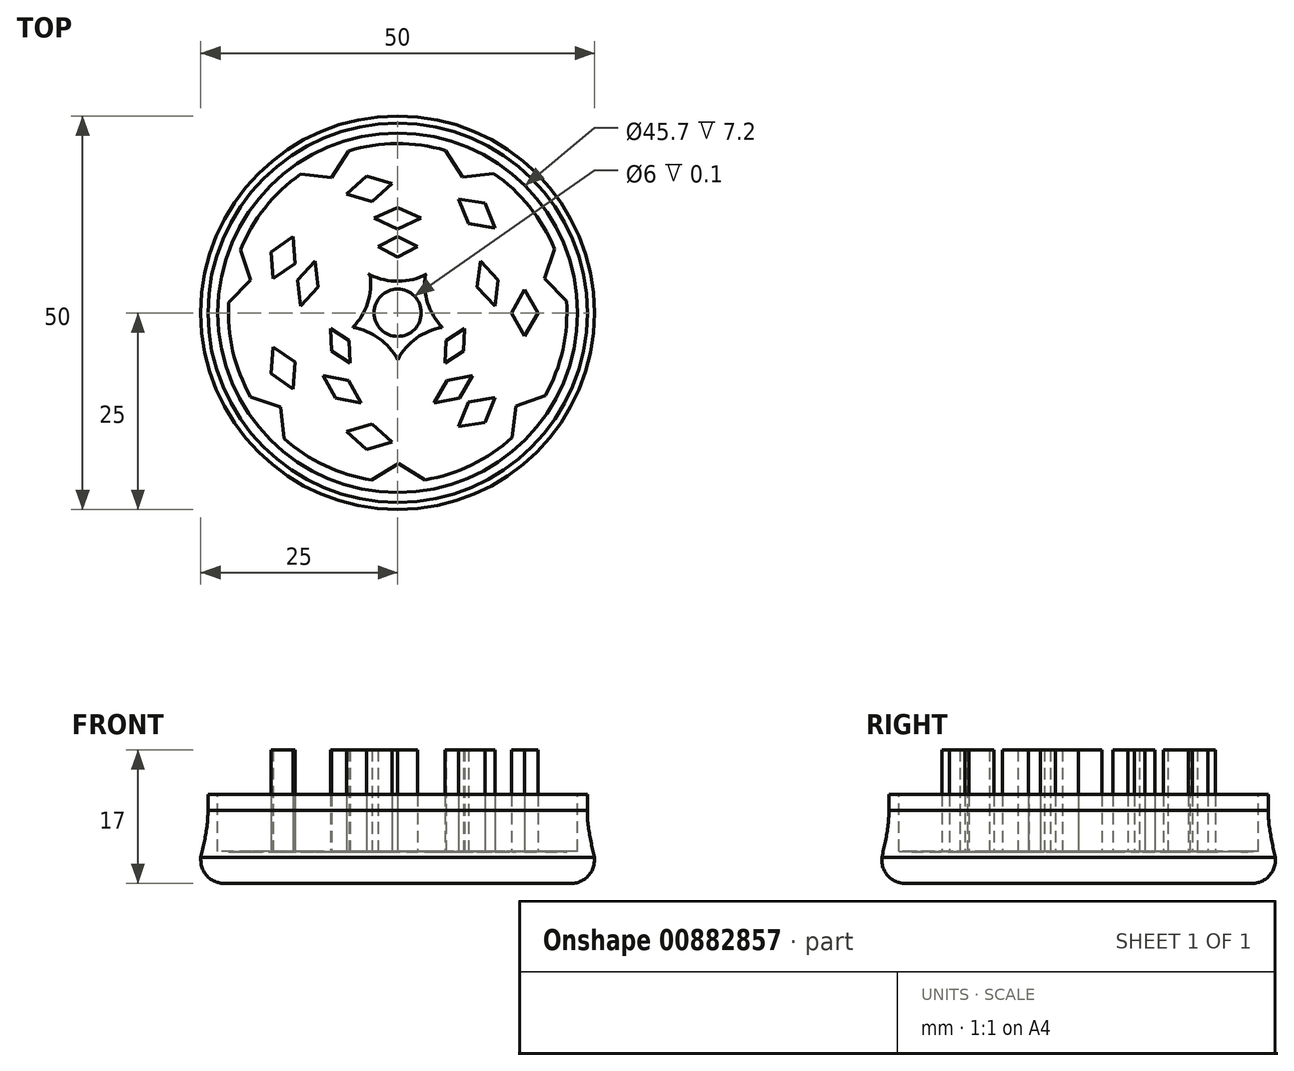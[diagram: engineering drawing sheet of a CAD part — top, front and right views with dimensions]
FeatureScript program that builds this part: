
annotation { "Feature Type Name" : "Feature", "Feature Type Description" : "" }
export const myFeature = defineFeature(function(context is Context, id is Id, definition is map)
    precondition{}
    {
        {
            var Q0;
            Q0=qCreatedBy(makeId("Top.planeOp"),FACE);
            var sketch = newSketch(context, id + "F0", { "sketchPlane" : qUnion([Q0])});
            skCircle(sketch, "E0", {"center": v(0, 0) * mm, "radius": 25 * mm});
            skSolve(sketch);
        }
        {
            var Q0;
            Q0 = qSketchRegion(id + "F0", true);
            extrude(context, id + "F1", {"entities" : qUnion([Q0]), "depth" : 15 * mm, "offsetDistance" : 25 * mm});
        }
        {
            var Q0;
            Q0=makeQuery(id+"F1.opExtrude","CAP_EDGE",EDGE,{"disambiguationData":[OSD([sQuery(id+"F0.wireOp",EDGE,"E0")])],"isStart":true});
            fillet(context, id + "F2", {"entities" : qUnion([Q0]), "radius" : 3 * mm, "tangentPropagation" : true, "allowEdgeOverflow" : false});
        }
        {
            var Q0;
            Q0=qCreatedBy(makeId("Front.planeOp"),FACE);
            var sketch = newSketch(context, id + "F3", { "sketchPlane" : qUnion([Q0])});
            skLineSegment(sketch, "E1", {"start": v(0, 23.25) * mm, "end": v(0, 17.15) * mm});
            skLineSegment(sketch, "E2", {"start": v(0, 17.15) * mm, "end": v(0, 14.94) * mm});
            skLineSegment(sketch, "E3", {"start": v(0, 14.94) * mm, "end": v(25, 14.94) * mm});
            skFitSpline(sketch, "E4", {"points": [v(25, 14.94) * mm, v(24.1, 9.2) * mm, v(25, 3.32) * mm], "startDerivative": vector(-2.73, -11.51) * mm, "endDerivative": vector(2.72, -11.72) * mm});
            skLineSegment(sketch, "E5", {"start": v(25, 3.32) * mm, "end": v(27.42, 5.28) * mm});
            skLineSegment(sketch, "E6", {"start": v(27.42, 5.28) * mm, "end": v(25, 14.94) * mm});
            skSolve(sketch);
        }
        {
            var Q0;
            Q0=makeQuery(id+"F3.imprint","IMPRINT",FACE,{"disambiguationData":[TD([[makeQuery(id+"F3.imprint","IMPRINT",EDGE,{"derivedFrom":sQuery(id+"F3.wireOp",EDGE,"E4")}),1.0]])]});
            var Q1;
            Q1=sQuery(id+"F3.wireOp",EDGE,"E1");
            revolve(context, id + "F4", {"operationType" : NewBodyOperationType.REMOVE, "surfaceOperationType" : NewSurfaceOperationType.NEW, "entities" : qUnion([Q0]), "axis" : qUnion([Q1]), "revolveType" : RevolveType.FULL, "oppositeDirection" : true});
        }
        {
            var Q0;
            Q0=makeQuery(id+"F1.opExtrude","CAP_FACE",FACE,{"disambiguationData":[OSD([sQuery(id+"F0.wireOp",EDGE,"E0")])],"isStart":false});
            var sketch = newSketch(context, id + "F5", { "sketchPlane" : qUnion([Q0])});
            skCircle(sketch, "E7", {"center": v(0, 0) * mm, "radius": 21.5 * mm});
            skSolve(sketch);
        }
        {
            var Q0;
            Q0 = qSketchRegion(id + "F5", true);
            extrude(context, id + "F6", {"entities" : qUnion([Q0]), "operationType" : NewBodyOperationType.REMOVE, "oppositeDirection" : true, "depth" : 11 * mm, "offsetDistance" : 25 * mm});
        }
        {
            var Q0;
            Q0=makeQuery(id+"F6.boolean.opBoolean","COPY",FACE,{"derivedFrom":makeQuery(id+"F6.opExtrude","CAP_FACE",FACE,{"disambiguationData":[OSD([sQuery(id+"F5.wireOp",EDGE,"E7")])],"isStart":false})});
            var sketch = newSketch(context, id + "F7", { "sketchPlane" : qUnion([Q0])});
            skCircle(sketch, "E8.cCircle", {"center": v(0, 0) * mm, "radius": 4.82 * mm, "construction": true});
            skLineSegment(sketch, "E8.0", {"start": v(-3.5, 4.82) * mm, "end": v(-3.5, 4.82) * mm});
            skLineSegment(sketch, "E8.1", {"start": v(3.5, 4.82) * mm, "end": v(3.5, 4.81) * mm});
            skLineSegment(sketch, "E8.2", {"start": v(5.66, -1.84) * mm, "end": v(5.66, -1.84) * mm});
            skLineSegment(sketch, "E8.3", {"start": v(0, -5.95) * mm, "end": v(-2.83, -3.9) * mm});
            skLineSegment(sketch, "E8.4", {"start": v(-5.66, -1.84) * mm, "end": v(-5.66, -1.83) * mm});
            skPoint(sketch, "E8.0.midPoint", {"position": v(0, 4.82) * mm});
            skCircle(sketch, "E9", {"center": v(0, 0) * mm, "radius": 3 * mm});
            skLineSegment(sketch, "E10", {"start": v(-3.69, 4.91) * mm, "end": v(-3.5, 4.82) * mm});
            skLineSegment(sketch, "E11", {"start": v(3.5, 4.82) * mm, "end": v(3.69, 4.91) * mm});
            skPoint(sketch, "E12.visualSharp", {"position": v(0, 3) * mm});
            skArc(sketch, "E12.filletArc", {"start": v(-3.69, 4.91) * mm, "mid": v(0, 4.01) * mm, "end": v(3.69, 4.91) * mm});
            skArc(sketch, "E13.1.0", {"start": v(-5.81, -1.99) * mm, "mid": v(-3.82, 1.24) * mm, "end": v(-3.53, 5.02) * mm});
            skArc(sketch, "E13.2.0", {"start": v(0.1, -6.14) * mm, "mid": v(-2.36, -3.25) * mm, "end": v(-5.87, -1.8) * mm});
            skArc(sketch, "E13.3.0", {"start": v(5.87, -1.8) * mm, "mid": v(2.36, -3.25) * mm, "end": v(-0.1, -6.14) * mm});
            skArc(sketch, "E13.4.0", {"start": v(3.53, 5.02) * mm, "mid": v(3.82, 1.24) * mm, "end": v(5.81, -1.99) * mm});
            skLineSegment(sketch, "E14.trimOffspring", {"start": v(4.58, 1.49) * mm, "end": v(5.66, -1.84) * mm});
            skLineSegment(sketch, "E15.trimOffspring", {"start": v(2.83, -3.9) * mm, "end": v(0, -5.95) * mm});
            skLineSegment(sketch, "E16.trimOffspring", {"start": v(-5.66, -1.84) * mm, "end": v(-5.66, -1.84) * mm});
            skLineSegment(sketch, "E17.trimOffspring", {"start": v(-4.58, 1.49) * mm, "end": v(-3.5, 4.82) * mm});
            skLineSegment(sketch, "E18", {"start": v(0, 0) * mm, "end": v(0, 12.01) * mm});
            skLineSegment(sketch, "E19", {"start": v(0, 12.01) * mm, "end": v(3, 12.01) * mm});
            skLineSegment(sketch, "E20", {"start": v(3, 12.01) * mm, "end": v(0, 10.64) * mm});
            skLineSegment(sketch, "E21.MirrorCS", {"start": v(3, 12.01) * mm, "end": v(0, 13.4) * mm});
            skLineSegment(sketch, "E22.MirrorCS", {"start": v(-3, 12.01) * mm, "end": v(0, 10.64) * mm});
            skLineSegment(sketch, "E23.MirrorCS", {"start": v(-3, 12.01) * mm, "end": v(0, 13.4) * mm});
            skLineSegment(sketch, "E24.1.0", {"start": v(-12.35, 0.86) * mm, "end": v(-10.12, 3.29) * mm});
            skLineSegment(sketch, "E24.1.1", {"start": v(-10.5, 6.57) * mm, "end": v(-10.12, 3.29) * mm});
            skLineSegment(sketch, "E24.1.2", {"start": v(-10.5, 6.57) * mm, "end": v(-12.74, 4.14) * mm});
            skLineSegment(sketch, "E24.1.3", {"start": v(-12.35, 0.86) * mm, "end": v(-12.74, 4.14) * mm});
            skLineSegment(sketch, "E24.2.0", {"start": v(-4.63, -11.48) * mm, "end": v(-6.25, -8.6) * mm});
            skLineSegment(sketch, "E24.2.1", {"start": v(-9.49, -7.96) * mm, "end": v(-6.25, -8.6) * mm});
            skLineSegment(sketch, "E24.2.2", {"start": v(-9.49, -7.96) * mm, "end": v(-7.87, -10.83) * mm});
            skLineSegment(sketch, "E24.2.3", {"start": v(-4.63, -11.48) * mm, "end": v(-7.87, -10.83) * mm});
            skLineSegment(sketch, "E24.3.0", {"start": v(9.49, -7.96) * mm, "end": v(6.25, -8.6) * mm});
            skLineSegment(sketch, "E24.3.1", {"start": v(4.63, -11.48) * mm, "end": v(6.25, -8.6) * mm});
            skLineSegment(sketch, "E24.3.2", {"start": v(4.63, -11.48) * mm, "end": v(7.87, -10.83) * mm});
            skLineSegment(sketch, "E24.3.3", {"start": v(9.49, -7.96) * mm, "end": v(7.87, -10.83) * mm});
            skLineSegment(sketch, "E24.4.0", {"start": v(10.5, 6.57) * mm, "end": v(10.12, 3.29) * mm});
            skLineSegment(sketch, "E24.4.1", {"start": v(12.35, 0.86) * mm, "end": v(10.12, 3.29) * mm});
            skLineSegment(sketch, "E24.4.2", {"start": v(12.35, 0.86) * mm, "end": v(12.74, 4.14) * mm});
            skLineSegment(sketch, "E24.4.3", {"start": v(10.5, 6.57) * mm, "end": v(12.74, 4.14) * mm});
            skLineSegment(sketch, "E25", {"start": v(0, 0) * mm, "end": v(0.1, -21.5) * mm});
            skLineSegment(sketch, "E26", {"start": v(0.1, -21.5) * mm, "end": v(3.92, -21.48) * mm});
            skLineSegment(sketch, "E27", {"start": v(3.92, -21.48) * mm, "end": v(0.08, -19.13) * mm});
            skLineSegment(sketch, "E28.MirrorCS", {"start": v(-3.73, -21.52) * mm, "end": v(0.08, -19.13) * mm});
            skLineSegment(sketch, "E29.MirrorCS", {"start": v(0.1, -21.5) * mm, "end": v(-3.73, -21.52) * mm});
            skLineSegment(sketch, "E30.1.0", {"start": v(19.24, -10.33) * mm, "end": v(15, -11.86) * mm});
            skLineSegment(sketch, "E30.1.1", {"start": v(14.5, -16.33) * mm, "end": v(15, -11.86) * mm});
            skLineSegment(sketch, "E30.1.2", {"start": v(16.87, -13.33) * mm, "end": v(19.24, -10.33) * mm});
            skLineSegment(sketch, "E30.1.3", {"start": v(16.87, -13.33) * mm, "end": v(14.5, -16.33) * mm});
            skLineSegment(sketch, "E30.2.0", {"start": v(20.07, 8.6) * mm, "end": v(18.63, 4.34) * mm});
            skLineSegment(sketch, "E30.2.1", {"start": v(21.8, 1.15) * mm, "end": v(18.63, 4.34) * mm});
            skLineSegment(sketch, "E30.2.2", {"start": v(20.94, 4.88) * mm, "end": v(20.07, 8.6) * mm});
            skLineSegment(sketch, "E30.2.3", {"start": v(20.94, 4.88) * mm, "end": v(21.8, 1.15) * mm});
            skLineSegment(sketch, "E30.3.0", {"start": v(5.8, 21.06) * mm, "end": v(8.22, 17.27) * mm});
            skLineSegment(sketch, "E30.3.1", {"start": v(12.7, 17.77) * mm, "end": v(8.22, 17.27) * mm});
            skLineSegment(sketch, "E30.3.2", {"start": v(9.24, 19.41) * mm, "end": v(5.8, 21.06) * mm});
            skLineSegment(sketch, "E30.3.3", {"start": v(9.24, 19.41) * mm, "end": v(12.7, 17.77) * mm});
            skLineSegment(sketch, "E30.4.0", {"start": v(-12.85, 17.66) * mm, "end": v(-8.37, 17.2) * mm});
            skLineSegment(sketch, "E30.4.1", {"start": v(-5.98, 21) * mm, "end": v(-8.37, 17.2) * mm});
            skLineSegment(sketch, "E30.4.2", {"start": v(-9.41, 19.33) * mm, "end": v(-12.85, 17.66) * mm});
            skLineSegment(sketch, "E30.4.3", {"start": v(-9.41, 19.33) * mm, "end": v(-5.98, 21) * mm});
            skLineSegment(sketch, "E30.5.0", {"start": v(-21.82, 0.96) * mm, "end": v(-18.67, 4.17) * mm});
            skLineSegment(sketch, "E30.5.1", {"start": v(-20.15, 8.42) * mm, "end": v(-18.67, 4.17) * mm});
            skLineSegment(sketch, "E30.5.2", {"start": v(-20.98, 4.7) * mm, "end": v(-21.82, 0.96) * mm});
            skLineSegment(sketch, "E30.5.3", {"start": v(-20.98, 4.7) * mm, "end": v(-20.15, 8.42) * mm});
            skLineSegment(sketch, "E30.6.0", {"start": v(-14.35, -16.46) * mm, "end": v(-14.9, -12) * mm});
            skLineSegment(sketch, "E30.6.1", {"start": v(-19.15, -10.5) * mm, "end": v(-14.9, -12) * mm});
            skLineSegment(sketch, "E30.6.2", {"start": v(-16.75, -13.48) * mm, "end": v(-14.35, -16.46) * mm});
            skLineSegment(sketch, "E30.6.3", {"start": v(-16.75, -13.48) * mm, "end": v(-19.15, -10.5) * mm});
            skSolve(sketch);
        }
        {
            var Q0;
            Q0 = qSketchRegion(id + "F7", true);
            extrude(context, id + "F8", {"entities" : qUnion([Q0]), "operationType" : NewBodyOperationType.ADD, "depth" : 10.8 * mm, "offsetDistance" : 25 * mm});
        }
        {
            var Q0;
            Q0=makeQuery(id+"F1.opExtrude","CAP_FACE",FACE,{"disambiguationData":[OSD([sQuery(id+"F0.wireOp",EDGE,"E0")])],"isStart":false});
            var sketch = newSketch(context, id + "F9", { "sketchPlane" : qUnion([Q0])});
            skCircle(sketch, "E31", {"center": v(0, 0) * mm, "radius": 26.73 * mm});
            skSolve(sketch);
        }
        {
            var Q0;
            Q0 = qSketchRegion(id + "F9", true);
            extrude(context, id + "F10", {"entities" : qUnion([Q0]), "operationType" : NewBodyOperationType.REMOVE, "oppositeDirection" : true, "depth" : 5.7 * mm, "offsetDistance" : 25 * mm});
        }
        {
            var Q0;
            Q0=makeQuery(id+"F10.boolean.opBoolean","COPY",FACE,{"disambiguationData":[TD([makeQuery(id+"F8.opExtrude","SWEPT_FACE",FACE,{"disambiguationData":[OSD([sQuery(id+"F7.wireOp",EDGE,"E9")])]})])],"derivedFrom":makeQuery(id+"F10.opExtrude","CAP_FACE",FACE,{"disambiguationData":[OSD([sQuery(id+"F9.wireOp",EDGE,"E31")])],"isStart":false})});
            var sketch = newSketch(context, id + "F11", { "sketchPlane" : qUnion([Q0])});
            skCircle(sketch, "E32", {"center": v(0, 0) * mm, "radius": 22.85 * mm});
            skSolve(sketch);
        }
        {
            var Q0;
            Q0=makeQuery(id+"F11.imprint","IMPRINT",FACE,{"disambiguationData":[TD([[makeQuery(id+"F11.imprint","IMPRINT",EDGE,{"derivedFrom":sQuery(id+"F11.wireOp",EDGE,"E32")}),1.0]])]});
            var Q1;
            {var subQ0=makeQuery(id+"F10.opExtrude","CAP_FACE",FACE,{"disambiguationData":[OSD([sQuery(id+"F9.wireOp",EDGE,"E31")])],"isStart":false});Q1=makeQuery(id+"F11.imprint","IMPRINT",FACE,{"disambiguationData":[TD([[makeQuery(id+"F11.imprint","IMPRINT",EDGE,{"derivedFrom":makeQuery(id+"F10.boolean.opBoolean","INTERSECT",EDGE,{"derivedFrom":[makeQuery(id+"F8.opExtrude","SWEPT_FACE",FACE,{"disambiguationData":[OSD([sQuery(id+"F7.wireOp",EDGE,"E9")])]}),subQ0]})}),-1.0]])]});}
            extrude(context, id + "F12", {"entities" : qUnion([Q0, Q1]), "operationType" : NewBodyOperationType.REMOVE, "oppositeDirection" : true, "depth" : 5.2 * mm, "offsetDistance" : 25 * mm});
        }
        {
            var Q0;
            {var subQ0=sQuery(id+"F5.wireOp",EDGE,"E7");Q0=makeQuery(id+"F8.boolean.opBoolean","SPLIT",FACE,{"disambiguationData":[TD([makeQuery(id+"F6.boolean.opBoolean","COPY",FACE,{"derivedFrom":makeQuery(id+"F6.opExtrude","SWEPT_FACE",FACE,{"disambiguationData":[OSD([subQ0])]})})])],"derivedFrom":makeQuery(id+"F6.boolean.opBoolean","COPY",FACE,{"derivedFrom":makeQuery(id+"F6.opExtrude","CAP_FACE",FACE,{"disambiguationData":[OSD([subQ0])],"isStart":false})})});}
            var sketch = newSketch(context, id + "F13", { "sketchPlane" : qUnion([Q0])});
            skCircle(sketch, "E33", {"center": v(0, 0) * mm, "radius": 6.14 * mm});
            skCircle(sketch, "E34", {"center": v(0, 0) * mm, "radius": 10.64 * mm});
            skCircle(sketch, "E35", {"center": v(0, 0) * mm, "radius": 13.4 * mm});
            skCircle(sketch, "E36", {"center": v(0, 0) * mm, "radius": 19.13 * mm});
            skLineSegment(sketch, "E37", {"start": v(0, 0) * mm, "end": v(0, 6.14) * mm});
            skLineSegment(sketch, "E38", {"start": v(0, 6.14) * mm, "end": v(0, 10.64) * mm});
            skLineSegment(sketch, "E39", {"start": v(0, 8.39) * mm, "end": v(2.5, 8.39) * mm});
            skLineSegment(sketch, "E40", {"start": v(2.5, 8.39) * mm, "end": v(0, 7.1) * mm});
            skLineSegment(sketch, "E41.MirrorCS", {"start": v(2.5, 8.39) * mm, "end": v(0, 9.67) * mm});
            skLineSegment(sketch, "E42.MirrorCS", {"start": v(-2.5, 8.39) * mm, "end": v(0, 9.67) * mm});
            skLineSegment(sketch, "E43.MirrorCS", {"start": v(-2.5, 8.39) * mm, "end": v(0, 7.1) * mm});
            skLineSegment(sketch, "E44.1.0", {"start": v(-6.02, -6.36) * mm, "end": v(-6.16, -3.55) * mm});
            skLineSegment(sketch, "E44.1.1", {"start": v(-8.52, -2.03) * mm, "end": v(-6.16, -3.55) * mm});
            skLineSegment(sketch, "E44.1.2", {"start": v(-6.02, -6.36) * mm, "end": v(-8.38, -4.84) * mm});
            skLineSegment(sketch, "E44.1.3", {"start": v(-8.52, -2.03) * mm, "end": v(-8.38, -4.84) * mm});
            skLineSegment(sketch, "E44.2.0", {"start": v(8.52, -2.03) * mm, "end": v(6.16, -3.55) * mm});
            skLineSegment(sketch, "E44.2.1", {"start": v(6.02, -6.36) * mm, "end": v(6.16, -3.55) * mm});
            skLineSegment(sketch, "E44.2.2", {"start": v(8.52, -2.03) * mm, "end": v(8.38, -4.84) * mm});
            skLineSegment(sketch, "E44.2.3", {"start": v(6.02, -6.36) * mm, "end": v(8.38, -4.84) * mm});
            skLineSegment(sketch, "E45", {"start": v(0, 0) * mm, "end": v(16.14, 0) * mm});
            skLineSegment(sketch, "E46", {"start": v(16.14, 0) * mm, "end": v(16.14, 2.95) * mm});
            skLineSegment(sketch, "E47", {"start": v(16.14, 2.95) * mm, "end": v(14.48, 0) * mm});
            skLineSegment(sketch, "E48.MirrorCS", {"start": v(16.14, 2.95) * mm, "end": v(17.81, 0) * mm});
            skLineSegment(sketch, "E49.MirrorCS", {"start": v(16.14, -2.95) * mm, "end": v(14.48, 0) * mm});
            skLineSegment(sketch, "E50.MirrorCS", {"start": v(16.14, -2.95) * mm, "end": v(17.81, 0) * mm});
            skLineSegment(sketch, "E51.1.0", {"start": v(7.76, 14.46) * mm, "end": v(9.03, 11.32) * mm});
            skLineSegment(sketch, "E51.1.1", {"start": v(12.37, 10.78) * mm, "end": v(9.03, 11.32) * mm});
            skLineSegment(sketch, "E51.1.2", {"start": v(12.37, 10.78) * mm, "end": v(11.1, 13.93) * mm});
            skLineSegment(sketch, "E51.1.3", {"start": v(7.76, 14.46) * mm, "end": v(11.1, 13.93) * mm});
            skLineSegment(sketch, "E51.2.0", {"start": v(-6.47, 15.08) * mm, "end": v(-3.22, 14.11) * mm});
            skLineSegment(sketch, "E51.2.1", {"start": v(-0.72, 16.4) * mm, "end": v(-3.22, 14.11) * mm});
            skLineSegment(sketch, "E51.2.2", {"start": v(-0.72, 16.4) * mm, "end": v(-3.96, 17.37) * mm});
            skLineSegment(sketch, "E51.2.3", {"start": v(-6.47, 15.08) * mm, "end": v(-3.96, 17.37) * mm});
            skLineSegment(sketch, "E51.3.0", {"start": v(-15.82, 4.35) * mm, "end": v(-13.04, 6.28) * mm});
            skLineSegment(sketch, "E51.3.1", {"start": v(-13.27, 9.66) * mm, "end": v(-13.04, 6.28) * mm});
            skLineSegment(sketch, "E51.3.2", {"start": v(-13.27, 9.66) * mm, "end": v(-16.05, 7.73) * mm});
            skLineSegment(sketch, "E51.3.3", {"start": v(-15.82, 4.35) * mm, "end": v(-16.05, 7.73) * mm});
            skLineSegment(sketch, "E51.4.0", {"start": v(-13.27, -9.66) * mm, "end": v(-13.04, -6.28) * mm});
            skLineSegment(sketch, "E51.4.1", {"start": v(-15.82, -4.35) * mm, "end": v(-13.04, -6.28) * mm});
            skLineSegment(sketch, "E51.4.2", {"start": v(-15.82, -4.35) * mm, "end": v(-16.05, -7.73) * mm});
            skLineSegment(sketch, "E51.4.3", {"start": v(-13.27, -9.66) * mm, "end": v(-16.05, -7.73) * mm});
            skLineSegment(sketch, "E51.5.0", {"start": v(-0.72, -16.4) * mm, "end": v(-3.22, -14.11) * mm});
            skLineSegment(sketch, "E51.5.1", {"start": v(-6.47, -15.08) * mm, "end": v(-3.22, -14.11) * mm});
            skLineSegment(sketch, "E51.5.2", {"start": v(-6.47, -15.08) * mm, "end": v(-3.96, -17.37) * mm});
            skLineSegment(sketch, "E51.5.3", {"start": v(-0.72, -16.4) * mm, "end": v(-3.96, -17.37) * mm});
            skLineSegment(sketch, "E51.6.0", {"start": v(12.37, -10.78) * mm, "end": v(9.03, -11.32) * mm});
            skLineSegment(sketch, "E51.6.1", {"start": v(7.76, -14.46) * mm, "end": v(9.03, -11.32) * mm});
            skLineSegment(sketch, "E51.6.2", {"start": v(7.76, -14.46) * mm, "end": v(11.1, -13.93) * mm});
            skLineSegment(sketch, "E51.6.3", {"start": v(12.37, -10.78) * mm, "end": v(11.1, -13.93) * mm});
            skSolve(sketch);
        }
        {
            var Q0;
            Q0=makeQuery(id+"F13.imprint","IMPRINT",FACE,{"disambiguationData":[TD([[makeQuery(id+"F13.imprint","IMPRINT",EDGE,{"derivedFrom":sQuery(id+"F13.wireOp",EDGE,"E44.1.0")}),1.0]])]});
            var Q1;
            {var subQ3=sQuery(id+"F13.wireOp",EDGE,"E42.MirrorCS");Q1=makeQuery(id+"F13.imprint","IMPRINT",FACE,{"disambiguationData":[TD([[makeQuery(id+"F13.imprint","IMPRINT",EDGE,{"derivedFrom":subQ3}),-1.0]])]});}
            var Q2;
            {var subQ0=sQuery(id+"F13.wireOp",EDGE,"E39");Q2=makeQuery(id+"F13.imprint","IMPRINT",FACE,{"disambiguationData":[TD([[makeQuery(id+"F13.imprint","IMPRINT",EDGE,{"derivedFrom":subQ0}),1.0]])]});}
            var Q3;
            {var subQ0=sQuery(id+"F13.wireOp",EDGE,"E39");Q3=makeQuery(id+"F13.imprint","IMPRINT",FACE,{"disambiguationData":[TD([[makeQuery(id+"F13.imprint","IMPRINT",EDGE,{"derivedFrom":subQ0}),-1.0]])]});}
            var Q4;
            Q4=makeQuery(id+"F13.imprint","IMPRINT",FACE,{"disambiguationData":[TD([[makeQuery(id+"F13.imprint","IMPRINT",EDGE,{"derivedFrom":sQuery(id+"F13.wireOp",EDGE,"E44.2.0")}),1.0]])]});
            var Q5;
            {var subQ1=sQuery(id+"F13.wireOp",EDGE,"E46");Q5=makeQuery(id+"F13.imprint","IMPRINT",FACE,{"disambiguationData":[TD([[makeQuery(id+"F13.imprint","IMPRINT",EDGE,{"derivedFrom":subQ1}),-1.0]])]});}
            var Q6;
            {var subQ0=sQuery(id+"F13.wireOp",EDGE,"E46");Q6=makeQuery(id+"F13.imprint","IMPRINT",FACE,{"disambiguationData":[TD([[makeQuery(id+"F13.imprint","IMPRINT",EDGE,{"derivedFrom":subQ0}),1.0]])]});}
            var Q7;
            Q7=makeQuery(id+"F13.imprint","IMPRINT",FACE,{"disambiguationData":[TD([[makeQuery(id+"F13.imprint","IMPRINT",EDGE,{"derivedFrom":sQuery(id+"F13.wireOp",EDGE,"E51.1.0")}),1.0]])]});
            var Q8;
            Q8=makeQuery(id+"F13.imprint","IMPRINT",FACE,{"disambiguationData":[TD([[makeQuery(id+"F13.imprint","IMPRINT",EDGE,{"derivedFrom":sQuery(id+"F13.wireOp",EDGE,"E51.2.0")}),1.0]])]});
            var Q9;
            Q9=makeQuery(id+"F13.imprint","IMPRINT",FACE,{"disambiguationData":[TD([[makeQuery(id+"F13.imprint","IMPRINT",EDGE,{"derivedFrom":sQuery(id+"F13.wireOp",EDGE,"E51.6.0")}),1.0]])]});
            var Q10;
            Q10=makeQuery(id+"F13.imprint","IMPRINT",FACE,{"disambiguationData":[TD([[makeQuery(id+"F13.imprint","IMPRINT",EDGE,{"derivedFrom":sQuery(id+"F13.wireOp",EDGE,"E51.5.0")}),1.0]])]});
            var Q11;
            Q11=makeQuery(id+"F13.imprint","IMPRINT",FACE,{"disambiguationData":[TD([[makeQuery(id+"F13.imprint","IMPRINT",EDGE,{"derivedFrom":sQuery(id+"F13.wireOp",EDGE,"E51.4.0")}),1.0]])]});
            var Q12;
            Q12=makeQuery(id+"F13.imprint","IMPRINT",FACE,{"disambiguationData":[TD([[makeQuery(id+"F13.imprint","IMPRINT",EDGE,{"derivedFrom":sQuery(id+"F13.wireOp",EDGE,"E51.3.0")}),1.0]])]});
            extrude(context, id + "F14", {"entities" : qUnion([Q0, Q1, Q2, Q3, Q4, Q5, Q6, Q7, Q8, Q9, Q10, Q11, Q12]), "operationType" : NewBodyOperationType.ADD, "depth" : 8 * mm, "offsetDistance" : 25 * mm});
        }
        {
            var Q0;
            Q0=makeQuery(id+"F14.opExtrude","CAP_FACE",FACE,{"disambiguationData":[OSD([sQuery(id+"F13.wireOp",EDGE,"E51.4.0"),sQuery(id+"F13.wireOp",EDGE,"E51.4.1"),sQuery(id+"F13.wireOp",EDGE,"E51.4.2"),sQuery(id+"F13.wireOp",EDGE,"E51.4.3")])],"isStart":false});
            var Q1;
            Q1=makeQuery(id+"F14.opExtrude","CAP_FACE",FACE,{"disambiguationData":[OSD([sQuery(id+"F13.wireOp",EDGE,"E44.1.0"),sQuery(id+"F13.wireOp",EDGE,"E44.1.1"),sQuery(id+"F13.wireOp",EDGE,"E44.1.2"),sQuery(id+"F13.wireOp",EDGE,"E44.1.3")])],"isStart":false});
            var Q2;
            Q2=makeQuery(id+"F14.opExtrude","CAP_FACE",FACE,{"disambiguationData":[OSD([sQuery(id+"F13.wireOp",EDGE,"E51.3.0"),sQuery(id+"F13.wireOp",EDGE,"E51.3.1"),sQuery(id+"F13.wireOp",EDGE,"E51.3.2"),sQuery(id+"F13.wireOp",EDGE,"E51.3.3")])],"isStart":false});
            var Q3;
            Q3=makeQuery(id+"F14.opExtrude","CAP_FACE",FACE,{"disambiguationData":[OSD([sQuery(id+"F13.wireOp",EDGE,"E51.2.0"),sQuery(id+"F13.wireOp",EDGE,"E51.2.1"),sQuery(id+"F13.wireOp",EDGE,"E51.2.2"),sQuery(id+"F13.wireOp",EDGE,"E51.2.3")])],"isStart":false});
            var Q4;
            Q4=makeQuery(id+"F14.opExtrude","CAP_FACE",FACE,{"disambiguationData":[OSD([sQuery(id+"F13.wireOp",EDGE,"E40"),sQuery(id+"F13.wireOp",EDGE,"E41.MirrorCS"),sQuery(id+"F13.wireOp",EDGE,"E42.MirrorCS"),sQuery(id+"F13.wireOp",EDGE,"E43.MirrorCS")])],"isStart":false});
            var Q5;
            Q5=makeQuery(id+"F14.opExtrude","CAP_FACE",FACE,{"disambiguationData":[OSD([sQuery(id+"F13.wireOp",EDGE,"E51.1.0"),sQuery(id+"F13.wireOp",EDGE,"E51.1.1"),sQuery(id+"F13.wireOp",EDGE,"E51.1.2"),sQuery(id+"F13.wireOp",EDGE,"E51.1.3")])],"isStart":false});
            var Q6;
            Q6=makeQuery(id+"F14.opExtrude","CAP_FACE",FACE,{"disambiguationData":[OSD([sQuery(id+"F13.wireOp",EDGE,"E47"),sQuery(id+"F13.wireOp",EDGE,"E48.MirrorCS"),sQuery(id+"F13.wireOp",EDGE,"E49.MirrorCS"),sQuery(id+"F13.wireOp",EDGE,"E50.MirrorCS")])],"isStart":false});
            var Q7;
            Q7=makeQuery(id+"F14.opExtrude","CAP_FACE",FACE,{"disambiguationData":[OSD([sQuery(id+"F13.wireOp",EDGE,"E44.2.0"),sQuery(id+"F13.wireOp",EDGE,"E44.2.1"),sQuery(id+"F13.wireOp",EDGE,"E44.2.2"),sQuery(id+"F13.wireOp",EDGE,"E44.2.3")])],"isStart":false});
            var Q8;
            Q8=makeQuery(id+"F14.opExtrude","CAP_FACE",FACE,{"disambiguationData":[OSD([sQuery(id+"F13.wireOp",EDGE,"E51.5.0"),sQuery(id+"F13.wireOp",EDGE,"E51.5.1"),sQuery(id+"F13.wireOp",EDGE,"E51.5.2"),sQuery(id+"F13.wireOp",EDGE,"E51.5.3")])],"isStart":false});
            var Q9;
            Q9=makeQuery(id+"F14.opExtrude","CAP_FACE",FACE,{"disambiguationData":[OSD([sQuery(id+"F13.wireOp",EDGE,"E51.6.0"),sQuery(id+"F13.wireOp",EDGE,"E51.6.1"),sQuery(id+"F13.wireOp",EDGE,"E51.6.2"),sQuery(id+"F13.wireOp",EDGE,"E51.6.3")])],"isStart":false});
            extrude(context, id + "F15", {"entities" : qUnion([Q0, Q1, Q2, Q3, Q4, Q5, Q6, Q7, Q8, Q9]), "operationType" : NewBodyOperationType.ADD, "depth" : 5 * mm, "offsetDistance" : 25 * mm});
        }
        {
            var Q0;
            Q0=makeQuery(id+"F10.boolean.opBoolean","COPY",FACE,{"disambiguationData":[TD([makeQuery(id+"F4.boolean.opBoolean","COPY",FACE,{"derivedFrom":makeQuery(id+"F4.opRevolve","SWEPT_FACE",FACE,{"disambiguationData":[OSD([sQuery(id+"F3.wireOp",EDGE,"E4")])]})})])],"derivedFrom":makeQuery(id+"F10.opExtrude","CAP_FACE",FACE,{"disambiguationData":[OSD([sQuery(id+"F9.wireOp",EDGE,"E31")])],"isStart":false})});
            extrude(context, id + "F16", {"entities" : qUnion([Q0]), "operationType" : NewBodyOperationType.ADD, "depth" : 2 * mm, "offsetDistance" : 25 * mm});
        }
    });
